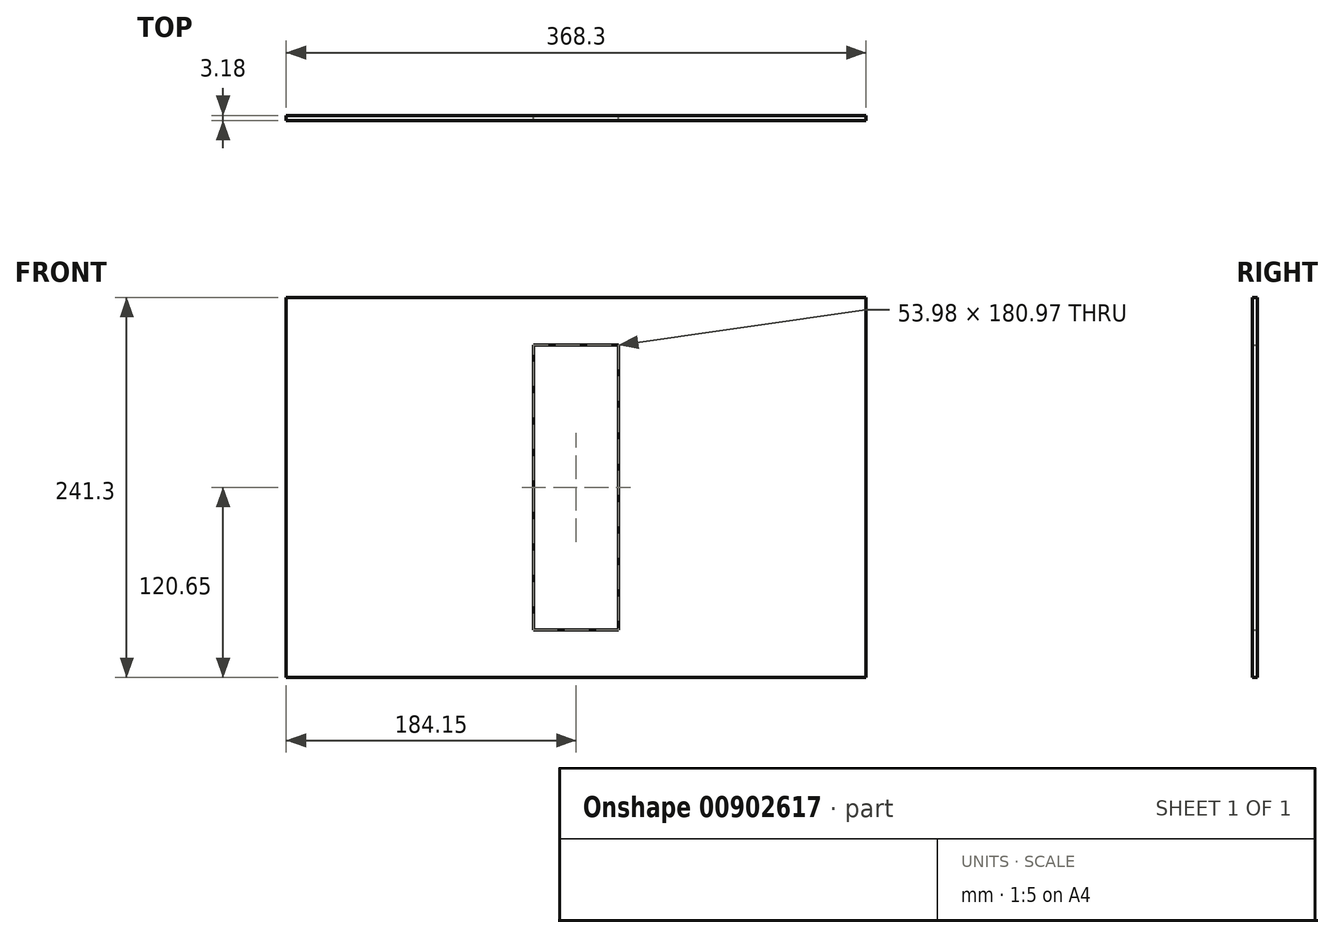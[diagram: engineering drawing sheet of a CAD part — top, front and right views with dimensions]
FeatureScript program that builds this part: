
annotation { "Feature Type Name" : "Feature", "Feature Type Description" : "" }
export const myFeature = defineFeature(function(context is Context, id is Id, definition is map)
    precondition{}
    {
        {
            var Q0;
            Q0=qCreatedBy(makeId("Front.planeOp"),FACE);
            var sketch = newSketch(context, id + "F0", { "sketchPlane" : qUnion([Q0])});
            skLineSegment(sketch, "E0.bottom", {"start": v(-184.15, -120.65) * mm, "end": v(184.15, -120.65) * mm});
            skLineSegment(sketch, "E0.top", {"start": v(-184.15, 120.65) * mm, "end": v(184.15, 120.65) * mm});
            skLineSegment(sketch, "E0.left", {"start": v(-184.15, -120.65) * mm, "end": v(-184.15, 120.65) * mm});
            skLineSegment(sketch, "E0.right", {"start": v(184.15, -120.65) * mm, "end": v(184.15, 120.65) * mm});
            skPoint(sketch, "E0.middle", {"position": v(0, 0) * mm});
            skLineSegment(sketch, "E1.bottom", {"start": v(-26.99, -90.49) * mm, "end": v(26.99, -90.49) * mm});
            skLineSegment(sketch, "E1.top", {"start": v(-26.99, 90.49) * mm, "end": v(26.99, 90.49) * mm});
            skLineSegment(sketch, "E1.left", {"start": v(-26.99, -90.49) * mm, "end": v(-26.99, 90.49) * mm});
            skLineSegment(sketch, "E1.right", {"start": v(26.99, -90.49) * mm, "end": v(26.99, 90.49) * mm});
            skSolve(sketch);
        }
        {
            var Q0;
            Q0=makeQuery(id+"F0.imprint","IMPRINT",FACE,{"disambiguationData":[TD([[makeQuery(id+"F0.imprint","IMPRINT",EDGE,{"derivedFrom":sQuery(id+"F0.wireOp",EDGE,"E0.bottom")}),1.0]])]});
            extrude(context, id + "F1", {"entities" : qUnion([Q0]), "endBound" : BoundingType.SYMMETRIC, "depth" : 3.17 * mm, "offsetDistance" : 25.4 * mm});
        }
    });
